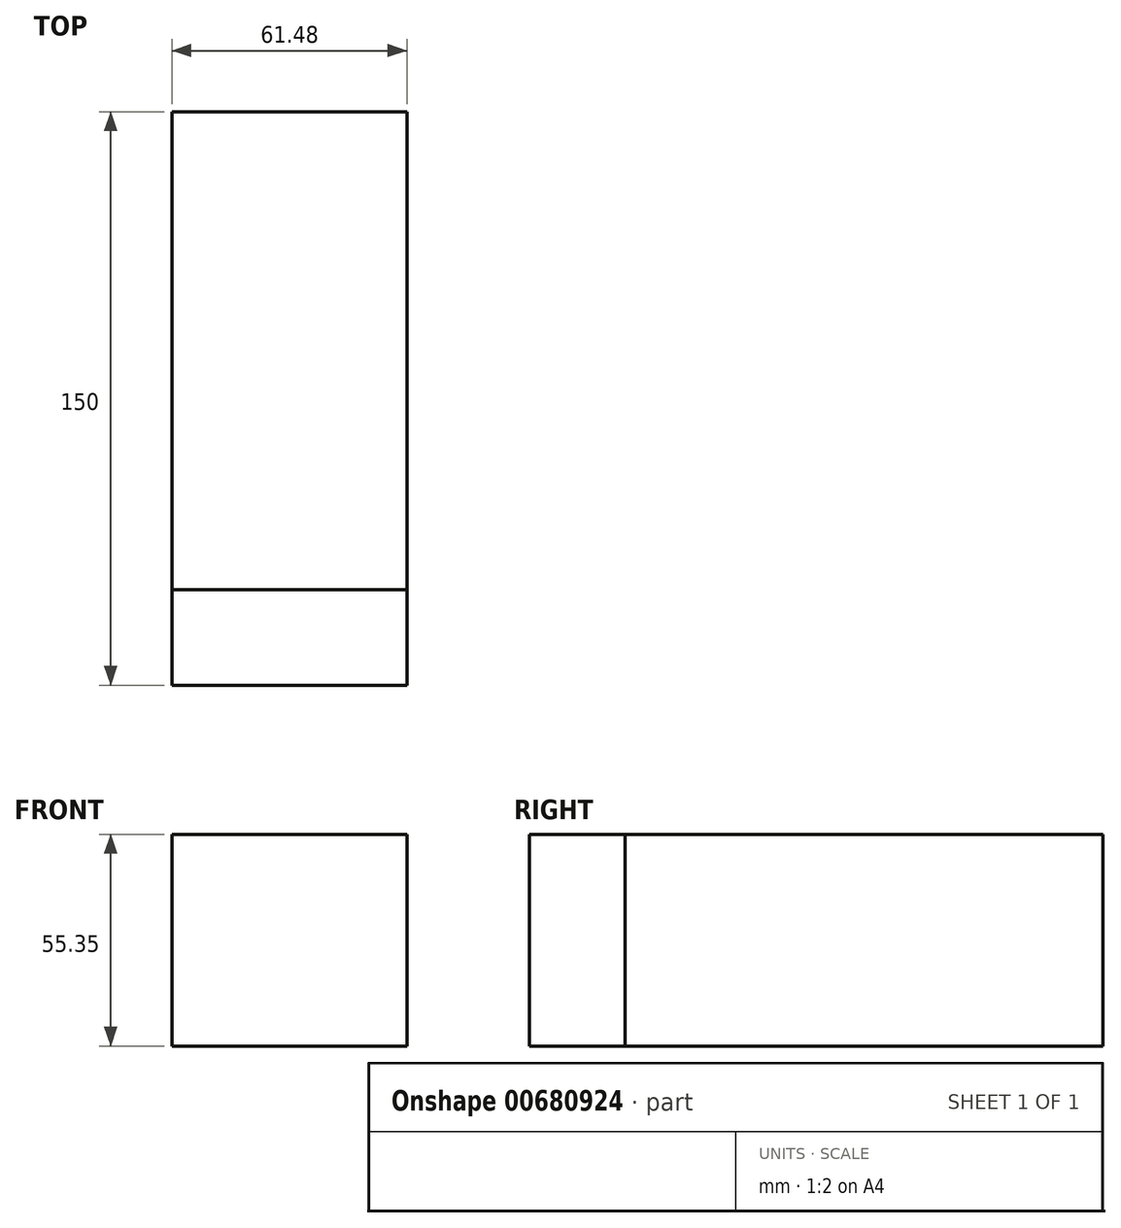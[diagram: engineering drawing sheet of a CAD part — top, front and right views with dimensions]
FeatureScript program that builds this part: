
annotation { "Feature Type Name" : "Feature", "Feature Type Description" : "" }
export const myFeature = defineFeature(function(context is Context, id is Id, definition is map)
    precondition{}
    {
        {
            var Q0;
            Q0=qCreatedBy(makeId("Front.planeOp"),FACE);
            var sketch = newSketch(context, id + "F0", { "sketchPlane" : qUnion([Q0])});
            skLineSegment(sketch, "E0.bottom", {"start": v(-26.25, 24.49) * mm, "end": v(35.23, 24.49) * mm});
            skLineSegment(sketch, "E0.top", {"start": v(-26.25, -30.86) * mm, "end": v(35.23, -30.86) * mm});
            skLineSegment(sketch, "E0.left", {"start": v(-26.25, 24.49) * mm, "end": v(-26.25, -30.86) * mm});
            skLineSegment(sketch, "E0.right", {"start": v(35.23, 24.49) * mm, "end": v(35.23, -30.86) * mm});
            skSolve(sketch);
        }
        {
            var Q0;
            Q0=makeQuery(id+"F0.imprint","IMPRINT",FACE,{"disambiguationData":[TD([[makeQuery(id+"F0.imprint","IMPRINT",EDGE,{"derivedFrom":sQuery(id+"F0.wireOp",EDGE,"E0.bottom")}),-1.0]])]});
            extrude(context, id + "F1", {"entities" : qUnion([Q0]), "depth" : 125 * mm, "offsetDistance" : 25 * mm});
        }
        {
            var Q0;
            Q0=makeQuery(id+"F1.opExtrude","CAP_FACE",FACE,{"disambiguationData":[OSD([sQuery(id+"F0.wireOp",EDGE,"E0.bottom"),sQuery(id+"F0.wireOp",EDGE,"E0.top"),sQuery(id+"F0.wireOp",EDGE,"E0.left"),sQuery(id+"F0.wireOp",EDGE,"E0.right")])],"isStart":false});
            extrude(context, id + "F2", {"entities" : qUnion([Q0]), "depth" : 25 * mm, "offsetDistance" : 25 * mm});
        }
    });
